# Revit family: HookSystem_HD10_EMCO
name_source: partatom
category: Generic Models
units: mm (PartAtom-declared; Revit-internal decimal feet)

## family parameters
Always vertical = Yes
Can host rebar = No
Cut with Voids When Loaded = No
Maintain Annotation Orientation = No
Part Type = Normal
Room Calculation Point = No
Round Connector Dimension = Use Diameter
Shared = No
Work Plane-Based = Yes

## types (4) — shared parameters
Assembly Code = E1090900
Construction Details = http://www.emcospi.com
Default Elevation = 4' - 0"
Depth = 0' - 0 5/8"
Height = 0' - 3 3/4"
Installation Phase = Closet and Utiity Shelving Hardware
Installation-Fabrication = http://www.emcospi.com
Keynote = 10 57 33
Manufacturer = EMCO Specialty Products, Inc.
Manufacturer Fax = 913-281-4554
Manufacturer Website = http://www.emcospi.com
Panel Material = EMCO - Light Oak Wood Panel
Product Data = http://www.emcospi.com
Product Properties = http://www.arcat.com
Sales Information = http://www.emcospi.com
Send Message = http://www.emcospi.com
Specification = http://www.emcospi.com
URL = https://www.arcat.com
Warranty Duration (Years) = 1

## per-type parameters (varying)
| type | Hook Count | Length | Model |
| EMCO D10 2 Hook Panel - 8" | 2 | 0' - 8" | D10 2 Hook Panel - 8" |
| EMCO D10 4 Hook Panel - 18" | 4 | 1' - 6" | D10 4 Hook Panel - 18" |
| EMCO D10 6 Hook Panel - 28" | 6 | 2' - 4" | D10 6 Hook Panel - 28" |
| EMCO D10 3 Hook Panel - 13" | 3 | 1' - 1" | D10 3 Hook Panel - 13" |

note: column(s) folded — value = type name in every type: Description

## geometry (parser evidence)
native form markers: Sweep x4
no freeform markers — native parametric forms only
